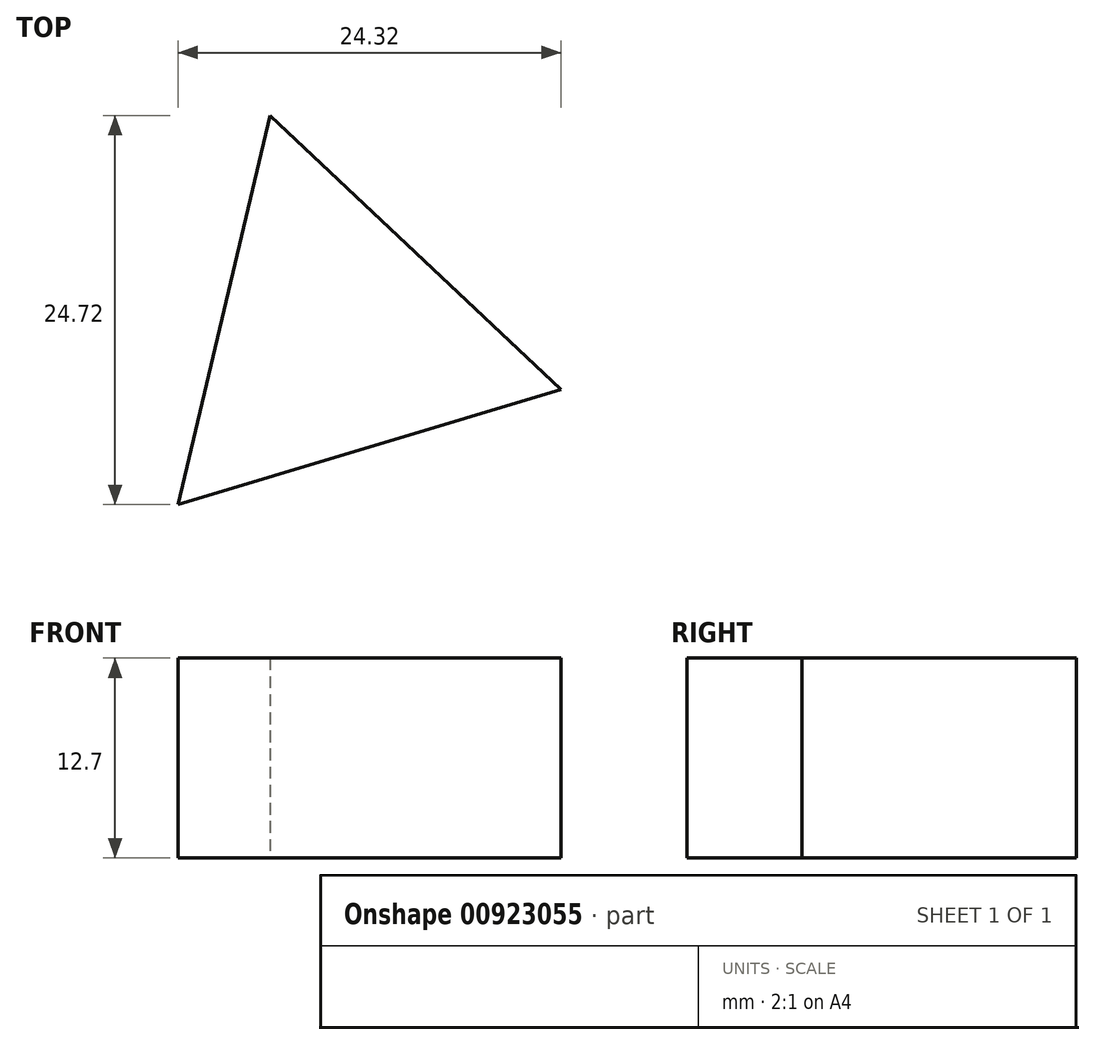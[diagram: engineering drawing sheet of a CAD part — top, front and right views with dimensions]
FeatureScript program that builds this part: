
annotation { "Feature Type Name" : "Feature", "Feature Type Description" : "" }
export const myFeature = defineFeature(function(context is Context, id is Id, definition is map)
    precondition{}
    {
        {
            var Q0;
            Q0=qCreatedBy(makeId("Top.planeOp"),FACE);
            var sketch = newSketch(context, id + "F0", { "sketchPlane" : qUnion([Q0])});
            skCircle(sketch, "E0.cCircle", {"center": v(0, 0) * mm, "radius": 7.33 * mm, "construction": true});
            skLineSegment(sketch, "E0.0", {"start": v(14.27, -3.37) * mm, "end": v(-10.05, -10.68) * mm});
            skLineSegment(sketch, "E0.1", {"start": v(-10.05, -10.68) * mm, "end": v(-4.22, 14.04) * mm});
            skLineSegment(sketch, "E0.2", {"start": v(-4.22, 14.04) * mm, "end": v(14.27, -3.37) * mm});
            skPoint(sketch, "E0.0.midPoint", {"position": v(2.11, -7.02) * mm});
            skSolve(sketch);
        }
        {
            var Q0;
            Q0=makeQuery(id+"F0.imprint","IMPRINT",FACE,{"disambiguationData":[TD([[makeQuery(id+"F0.imprint","IMPRINT",EDGE,{"derivedFrom":sQuery(id+"F0.wireOp",EDGE,"E0.0")}),-1.0]])]});
            extrude(context, id + "F1", {"entities" : qUnion([Q0]), "depth" : 12.7 * mm, "offsetDistance" : 25.4 * mm});
        }
    });
